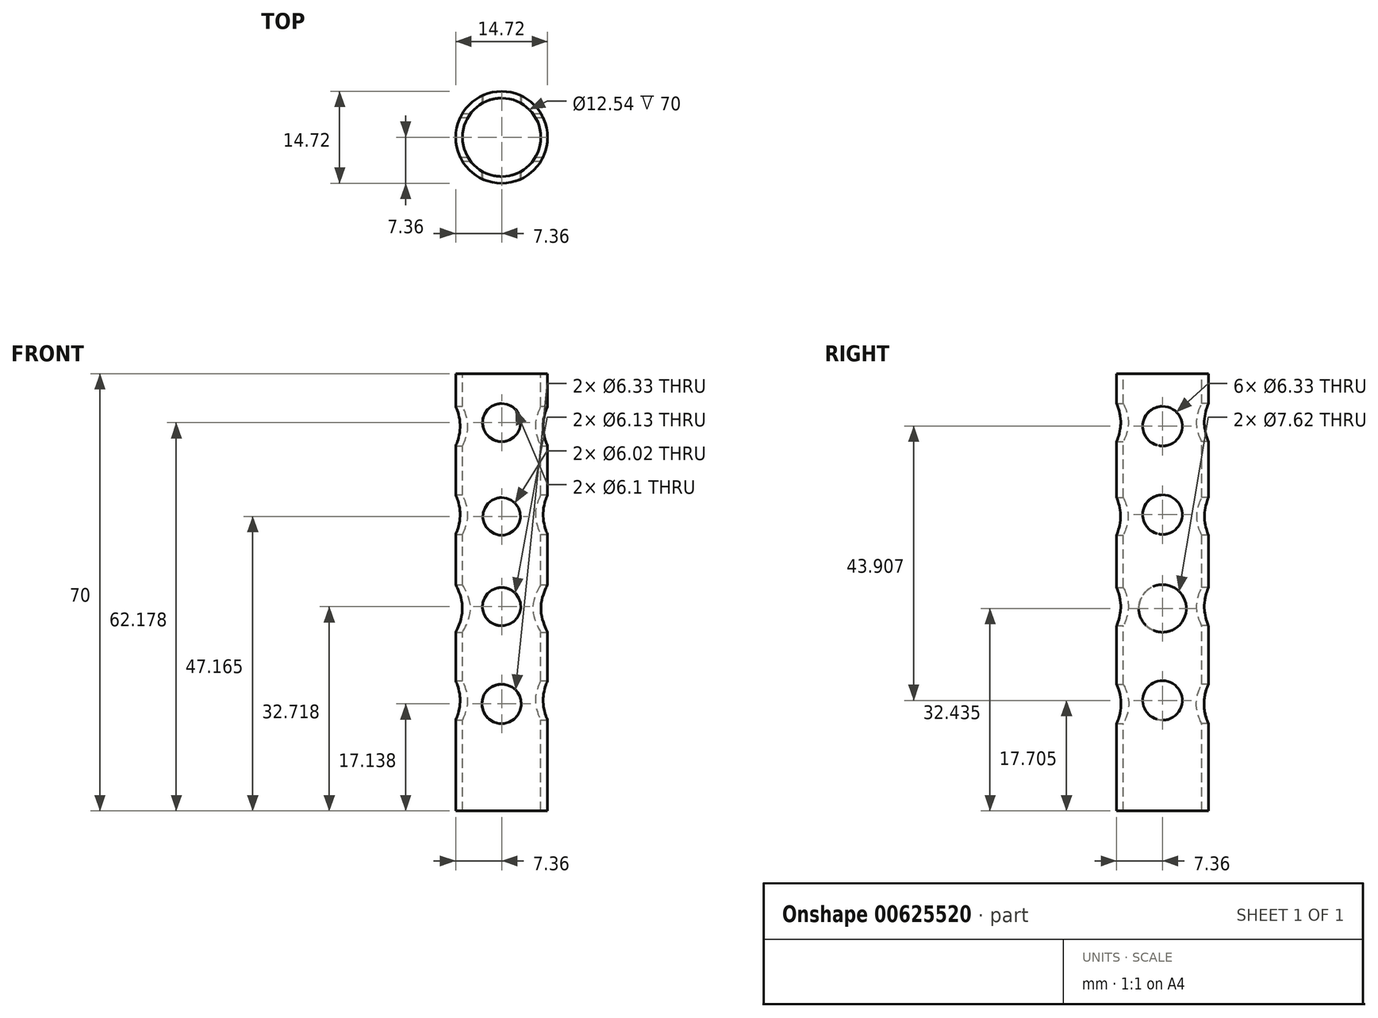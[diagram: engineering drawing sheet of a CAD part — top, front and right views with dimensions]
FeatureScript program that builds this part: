
annotation { "Feature Type Name" : "Feature", "Feature Type Description" : "" }
export const myFeature = defineFeature(function(context is Context, id is Id, definition is map)
    precondition{}
    {
        {
            var Q0;
            Q0=qCreatedBy(makeId("Top.planeOp"),FACE);
            var sketch = newSketch(context, id + "F0", { "sketchPlane" : qUnion([Q0])});
            skCircle(sketch, "E0", {"center": v(0, 0) * mm, "radius": 7.36 * mm});
            skSolve(sketch);
        }
        {
            var Q0;
            Q0=makeQuery(id+"F0.imprint","IMPRINT",FACE,{"disambiguationData":[TD([[makeQuery(id+"F0.imprint","IMPRINT",EDGE,{"derivedFrom":sQuery(id+"F0.wireOp",EDGE,"E0")}),1.0]])]});
            extrude(context, id + "F1", {"entities" : qUnion([Q0]), "depth" : 70 * mm, "offsetDistance" : 25 * mm});
        }
        {
            var Q0;
            Q0=qCreatedBy(makeId("Right.planeOp"),FACE);
            var sketch = newSketch(context, id + "F2", { "sketchPlane" : qUnion([Q0])});
            skCircle(sketch, "E1", {"center": v(0, 61.61) * mm, "radius": 3.17 * mm});
            skCircle(sketch, "E2", {"center": v(0, 47.45) * mm, "radius": 3.17 * mm});
            skCircle(sketch, "E3", {"center": v(0, 32.43) * mm, "radius": 3.81 * mm});
            skCircle(sketch, "E4", {"center": v(0, 17.7) * mm, "radius": 3.17 * mm});
            skSolve(sketch);
        }
        {
            var Q0;
            Q0 = qSketchRegion(id + "F2", true);
            extrude(context, id + "F3", {"entities" : qUnion([Q0]), "operationType" : NewBodyOperationType.REMOVE, "oppositeDirection" : true, "depth" : 14.8 * mm, "offsetDistance" : 25 * mm});
        }
        {
            var Q0;
            Q0 = qSketchRegion(id + "F2", true);
            extrude(context, id + "F4", {"entities" : qUnion([Q0]), "operationType" : NewBodyOperationType.REMOVE, "depth" : 35.1 * mm, "offsetDistance" : 25 * mm});
        }
        {
            var Q0;
            Q0=makeQuery(id+"F1.opExtrude","CAP_FACE",FACE,{"disambiguationData":[OSD([sQuery(id+"F0.wireOp",EDGE,"E0")])],"isStart":false});
            var sketch = newSketch(context, id + "F5", { "sketchPlane" : qUnion([Q0])});
            skCircle(sketch, "E5", {"center": v(0, 0) * mm, "radius": 6.27 * mm});
            skSolve(sketch);
        }
        {
            var Q0;
            Q0=makeQuery(id+"F5.imprint","IMPRINT",FACE,{"disambiguationData":[TD([[makeQuery(id+"F5.imprint","IMPRINT",EDGE,{"derivedFrom":sQuery(id+"F5.wireOp",EDGE,"E5")}),1.0]])]});
            extrude(context, id + "F6", {"entities" : qUnion([Q0]), "operationType" : NewBodyOperationType.REMOVE, "oppositeDirection" : true, "depth" : 105 * mm, "offsetDistance" : 25 * mm});
        }
        {
            var Q0;
            Q0=qCreatedBy(makeId("Front.planeOp"),FACE);
            var sketch = newSketch(context, id + "F7", { "sketchPlane" : qUnion([Q0])});
            skCircle(sketch, "E6", {"center": v(0, 62.18) * mm, "radius": 3.05 * mm});
            skCircle(sketch, "E7", {"center": v(0, 47.17) * mm, "radius": 3.01 * mm});
            skCircle(sketch, "E8", {"center": v(0, 32.72) * mm, "radius": 3.06 * mm});
            skCircle(sketch, "E9", {"center": v(0, 17.14) * mm, "radius": 3.17 * mm});
            skSolve(sketch);
        }
        {
            var Q0;
            Q0 = qSketchRegion(id + "F7", true);
            extrude(context, id + "F8", {"entities" : qUnion([Q0]), "operationType" : NewBodyOperationType.REMOVE, "oppositeDirection" : true, "depth" : 25 * mm, "offsetDistance" : 25 * mm});
        }
        {
            var Q0;
            Q0 = qSketchRegion(id + "F7", true);
            extrude(context, id + "F9", {"entities" : qUnion([Q0]), "operationType" : NewBodyOperationType.REMOVE, "depth" : 36.2 * mm, "offsetDistance" : 25 * mm});
        }
    });
